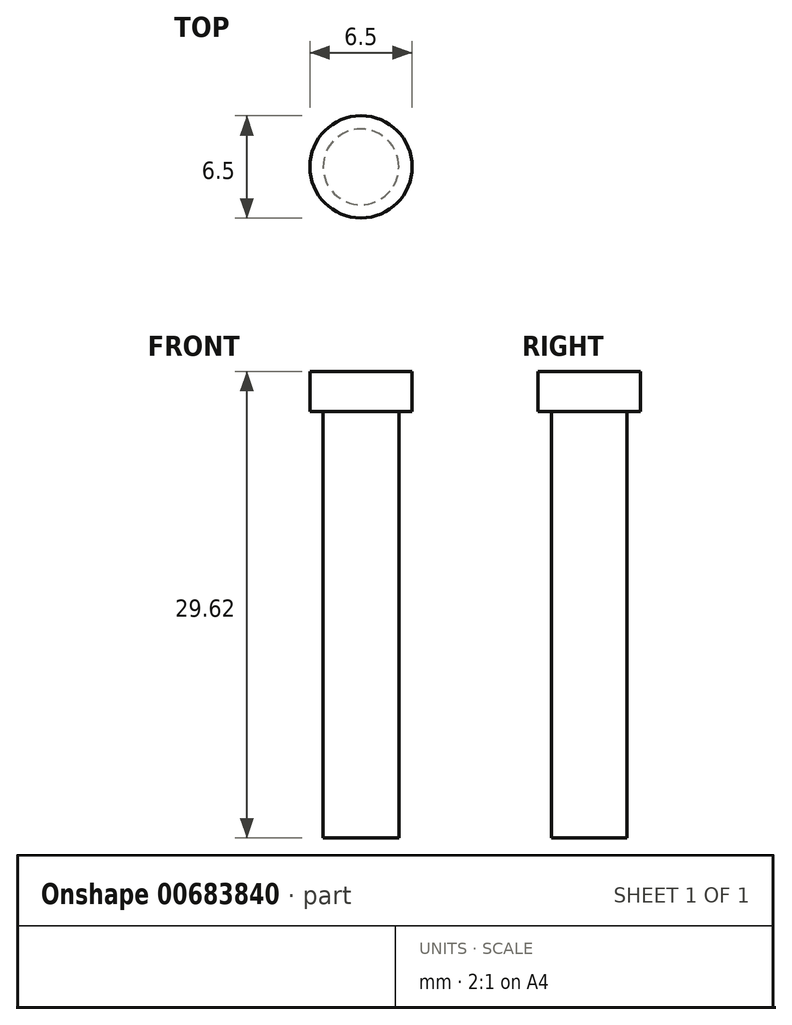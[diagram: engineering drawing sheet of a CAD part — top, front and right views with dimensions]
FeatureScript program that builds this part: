
annotation { "Feature Type Name" : "Feature", "Feature Type Description" : "" }
export const myFeature = defineFeature(function(context is Context, id is Id, definition is map)
    precondition{}
    {
        {
            var Q0;
            Q0=qCreatedBy(makeId("Top.planeOp"),FACE);
            var sketch = newSketch(context, id + "F0", { "sketchPlane" : qUnion([Q0])});
            skCircle(sketch, "E0", {"center": v(0, 0) * mm, "radius": 2.4 * mm});
            skSolve(sketch);
        }
        {
            var Q0;
            Q0=makeQuery(id+"F0.imprint","IMPRINT",FACE,{"disambiguationData":[TD([[makeQuery(id+"F0.imprint","IMPRINT",EDGE,{"derivedFrom":sQuery(id+"F0.wireOp",EDGE,"E0")}),1.0]])]});
            extrude(context, id + "F1", {"entities" : qUnion([Q0]), "depth" : 13.54 * mm, "offsetDistance" : 25.4 * mm, "hasSecondDirection" : true, "secondDirectionOppositeDirection" : true, "secondDirectionDepth" : 13.54 * mm});
        }
        {
            var Q0;
            Q0=makeQuery(id+"F1.opExtrude","CAP_FACE",FACE,{"disambiguationData":[OSD([sQuery(id+"F0.wireOp",EDGE,"E0")])],"isStart":false});
            var sketch = newSketch(context, id + "F2", { "sketchPlane" : qUnion([Q0])});
            skCircle(sketch, "E1", {"center": v(0, 0) * mm, "radius": 3.25 * mm});
            skSolve(sketch);
        }
        {
            var Q0;
            Q0 = qSketchRegion(id + "F2", true);
            extrude(context, id + "F3", {"entities" : qUnion([Q0]), "operationType" : NewBodyOperationType.ADD, "depth" : 2.54 * mm, "offsetDistance" : 25.4 * mm});
        }
    });
